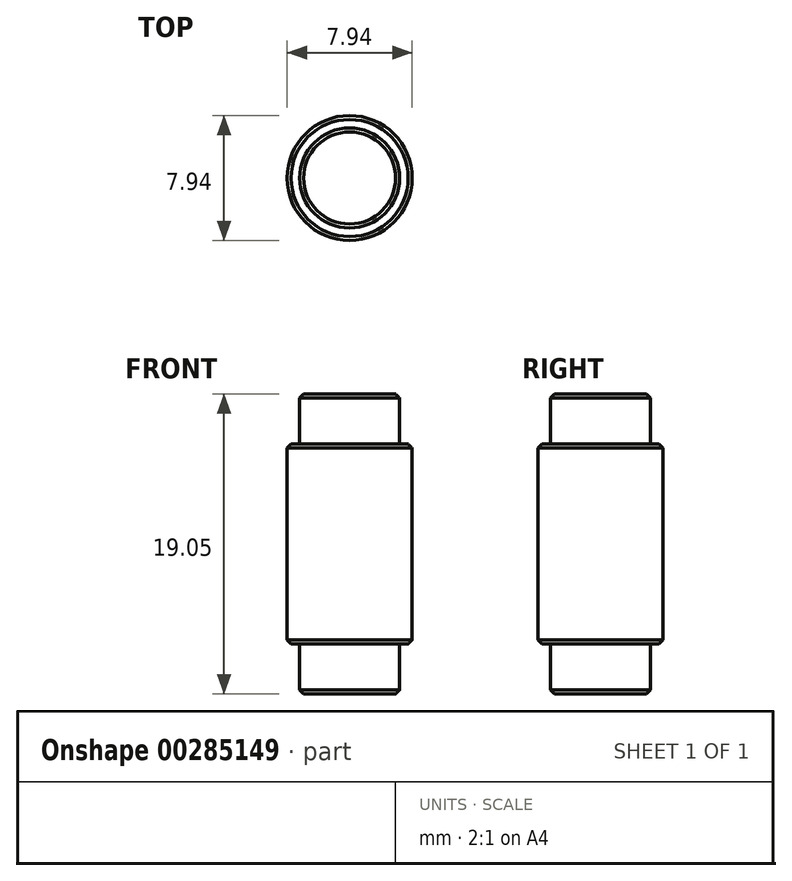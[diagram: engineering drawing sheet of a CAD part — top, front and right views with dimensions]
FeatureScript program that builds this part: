
annotation { "Feature Type Name" : "Feature", "Feature Type Description" : "" }
export const myFeature = defineFeature(function(context is Context, id is Id, definition is map)
    precondition{}
    {
        {
            var Q0;
            Q0=qCreatedBy(makeId("Top.planeOp"),FACE);
            var sketch = newSketch(context, id + "F0", { "sketchPlane" : qUnion([Q0])});
            skCircle(sketch, "E0", {"center": v(0, 0) * mm, "radius": 3.18 * mm});
            skCircle(sketch, "E1", {"center": v(0, 0) * mm, "radius": 3.97 * mm});
            skSolve(sketch);
        }
        {
            var Q0;
            Q0=makeQuery(id+"F0.imprint","IMPRINT",FACE,{"disambiguationData":[TD([[makeQuery(id+"F0.imprint","IMPRINT",EDGE,{"derivedFrom":sQuery(id+"F0.wireOp",EDGE,"E0")}),1.0]])]});
            extrude(context, id + "F1", {"entities" : qUnion([Q0]), "depth" : 19.05 * mm});
        }
        {
            var Q0;
            Q0=makeQuery(id+"F1.opExtrude","CAP_FACE",FACE,{"disambiguationData":[OSD([sQuery(id+"F0.wireOp",EDGE,"E0")])],"isStart":false});
            cPlane(context, id + "F2", {"entities" : qUnion([Q0]), "cplaneType" : CPlaneType.OFFSET, "offset" : 3.17 * mm, "oppositeDirection" : true, "width" : 152.4 * mm, "height" : 152.4 * mm});
        }
        {
            var Q0;
            Q0=qCreatedBy(id+"F2.planeOp",FACE);
            var sketch = newSketch(context, id + "F3", { "sketchPlane" : qUnion([Q0])});
            skCircle(sketch, "E2", {"center": v(0, 0) * mm, "radius": 3.97 * mm});
            skSolve(sketch);
        }
        {
            var Q0;
            Q0 = qSketchRegion(id + "F3", true);
            extrude(context, id + "F4", {"entities" : qUnion([Q0]), "operationType" : NewBodyOperationType.ADD, "oppositeDirection" : true, "depth" : 12.7 * mm});
        }
        {
            var Q0;
            Q0=makeQuery(id+"F1.opExtrude","CAP_EDGE",EDGE,{"disambiguationData":[OSD([sQuery(id+"F0.wireOp",EDGE,"E0")])],"isStart":false});
            var Q1;
            Q1=makeQuery(id+"F4.opExtrude","CAP_EDGE",EDGE,{"disambiguationData":[OSD([sQuery(id+"F3.wireOp",EDGE,"E2")])],"isStart":true});
            var Q2;
            Q2=makeQuery(id+"F4.opExtrude","CAP_EDGE",EDGE,{"disambiguationData":[OSD([sQuery(id+"F3.wireOp",EDGE,"E2")])],"isStart":false});
            var Q3;
            Q3=makeQuery(id+"F1.opExtrude","CAP_EDGE",EDGE,{"disambiguationData":[OSD([sQuery(id+"F0.wireOp",EDGE,"E0")])],"isStart":true});
            chamfer(context, id + "F5", {"entities" : qUnion([Q0, Q1, Q2, Q3]), "width" : 0.25 * mm, "tangentPropagation" : true});
        }
    });
